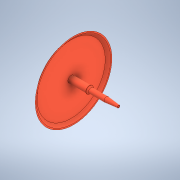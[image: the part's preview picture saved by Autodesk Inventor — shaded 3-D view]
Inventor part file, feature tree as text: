
AUTODESK INVENTOR PART (.ipt)
format: ipt  version: 2020 (Build 240168000, 168)  size: 211,968 bytes
history: native  units: mm
features: sketch x12, extrude x8, revolve x3, fillet x3, plane x1, chamfer x1
ambient origin geometry x8: Origin, YZ Plane, XZ Plane, XY Plane, X Axis, Y Axis, Z Axis, Center Point
bodies: Solid1 (feature_tree)
feature tree (28):
  extrude  "Extrusion1"  Depth=28.0mm
  plane  "Work Plane1"
  sketch  "Sketch2"  dims[d2=0.4mm d3=0.0mm d4=2.0mm]
  revolve  "Revolution1"  [1 undecoded]
  extrude  "Extrusion2"  TaperAngle=90.0deg  [1 undecoded]
  fillet  "Fillet1"  Radius=9.0mm
  extrude  "Extrusion3"  Depth=2.0mm
  extrude  "Extrusion4"  Depth=3.0mm TaperAngle=0.0deg
  extrude  "Extrusion5"  Depth=7.5mm TaperAngle=0.0deg
  extrude  "Extrusion6"  Depth=3.0mm TaperAngle=0.0deg
  chamfer  "Chamfer1"  Distance=11.86mm
  revolve  "Revolution2"  [1 undecoded]
  extrude  "Extrusion7"  TaperAngle=90.0deg  [1 undecoded]
  fillet  "Fillet2"  Radius=0.8mm
  extrude  "Extrusion8"  Depth=0.1mm
  fillet  "Fillet3"  Radius=6.5mm
  revolve  "Revolution3"  [1 undecoded]
  sketch  "Sketch1"  dims[d0=34.0mm d1=28.0mm]
  sketch  "Sketch3"  dims[d5=34.0mm d6=90.0deg d7=9.0mm]
  sketch  "Sketch4"  dims[d8=0.6mm d9=0.0mm d10=2.0mm]
  sketch  "Sketch5"  dims[d11=2.0mm d12=3.0mm d13=0.0mm]
  sketch  "Sketch6"  dims[d14=2.7mm d15=7.5mm d16=0.0mm]
  sketch  "Sketch7"  dims[d17=3.0mm d18=0.14mm d19=0.0mm]
  sketch  "Sketch8"  dims[d20=2.0mm d21=11.86mm d22=0.0mm]
  sketch  "Sketch9"  dims[d23=0.5mm d24=2.0mm d25=45.0deg d26=0.5mm]
  sketch  "Sketch10"  dims[d27=5.0mm d28=90.0deg d29=0.8mm]
  sketch  "Sketch11"  dims[d30=0.1mm d31=0.0mm d32=0.1mm d33=6.5mm]
  sketch  "Sketch12"  dims[d34=0.1mm d35=0.0mm d36=0.1mm d37=1.0mm d38=90.0deg]
note: 5 required parameter values undecoded (feature->parameter linkage not recoverable at this tier; creation-order binding heuristic only, values carry confidence <= 0.55)